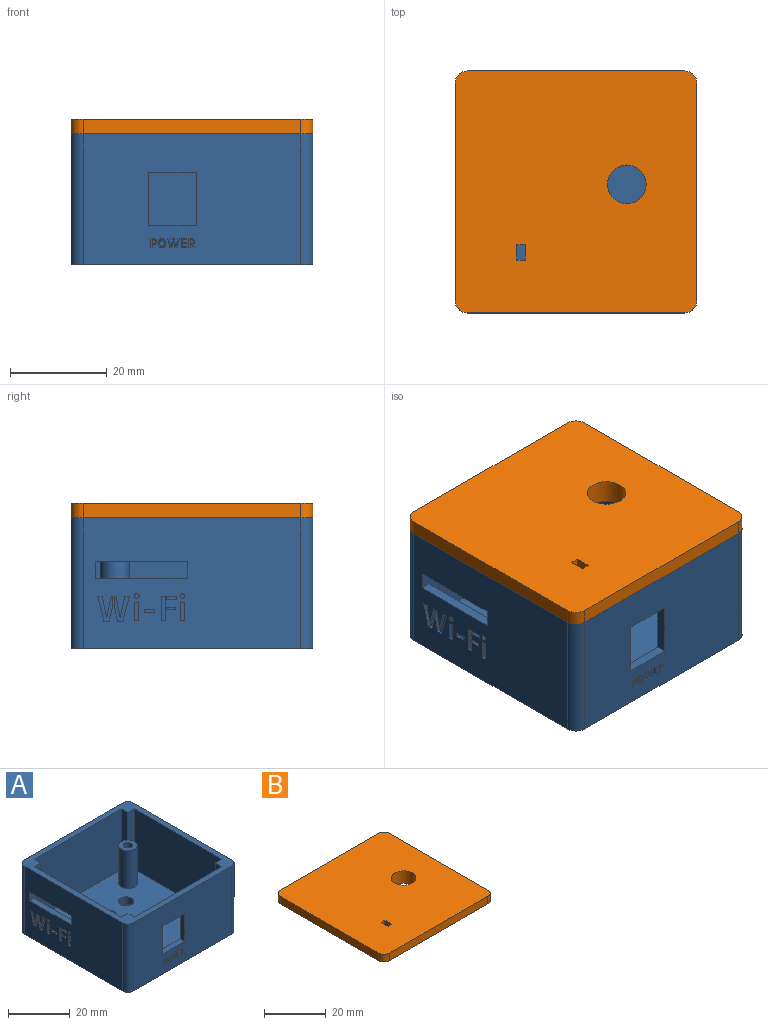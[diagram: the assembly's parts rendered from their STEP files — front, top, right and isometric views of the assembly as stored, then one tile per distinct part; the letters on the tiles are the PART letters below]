
ASSEMBLY  parts=2 mates=1
PART A: 250 faces, bbox 50x50x27 mm
  f0: plane 45x27mm, normal (-1,0,0), area 1117.5mm2, adj f4,f8,f18,f29,f30,f31,f40,f43
  f1: plane 45x27mm, normal (0,-1,0), area 1099.5mm2, adj f4,f8,f25,f26,f27,f28,f40,f41
  f2: plane 40x24mm, normal (1,0,0), area 893.5mm2, adj f4,f11,f17,f18,f29,f30,f31
  f3: plane 24x3mm, normal (1,0,0), area 72mm2, adj f4,f11,f13,f18
  f4: plane 50x50mm, normal (0,0,1), area 414.6mm2, adj f0,f1,f2,f3,f5,f6,f7,f9
  f5: plane 24x3mm, normal (-1,0,0), area 72mm2, adj f4,f11,f13,f16
  f6: plane 45x27mm, normal (1,0,0), area 1215mm2, adj f4,f8,f41,f42
  f7: plane 45x27mm, normal (0,1,0), area 1215mm2, adj f4,f8,f42,f43
  f8: plane 50x50mm, normal (0,0,-1), area 2376.9mm2, adj f0,f1,f6,f7,f32,f33,f34,f35
  f9: plane 24x3mm, normal (1,0,0), area 72mm2, adj f4,f11,f12,f17
  f10: plane 24x3mm, normal (-1,0,0), area 72mm2, adj f4,f11,f12,f14
  f11: plane 46x46mm, normal (0,0,1), area 1962.2mm2, adj f2,f3,f5,f9,f10,f12,f13,f14
  f12: plane 40x24mm, normal (0,1,0), area 851.1mm2, adj f4,f9,f10,f11,f25,f26,f27,f28
  f13: plane 40x24mm, normal (0,-1,0), area 960mm2, adj f3,f4,f5,f11
  f14: plane 24x3mm, normal (0,1,0), area 72mm2, adj f4,f10,f11,f15
  f15: plane 40x24mm, normal (-1,0,0), area 960mm2, adj f4,f11,f14,f16
  f16: plane 24x3mm, normal (0,-1,0), area 72mm2, adj f4,f5,f11,f15
  f17: plane 24x3mm, normal (0,1,0), area 72mm2, adj f2,f4,f9,f11
  f18: plane 24x5mm, normal (0,-1,0), area 79mm2, adj f0,f2,f3,f4,f11,f29,f31
  f19: cylinder r=1.5mm len=16.5mm, axis (0,0,-1), area 155.5mm2, adj f21,f38
  f20: cylinder r=3mm len=15mm, axis (0,0,-1), area 282.7mm2, adj f11,f21
  f21: plane 6x6mm, normal (0,0,1), area 21.2mm2, adj f19,f20
  f22: cylinder r=1.5mm len=16.5mm, axis (0,0,-1), area 155.5mm2, adj f24,f39
  f23: cylinder r=3mm len=15mm, axis (0,0,-1), area 282.7mm2, adj f11,f24
  f24: plane 6x6mm, normal (0,0,1), area 21.2mm2, adj f22,f23
  f25: plane 11x2mm, normal (1,0,0), area 22mm2, adj f1,f12,f26,f28
  f26: plane 9.9x2mm, normal (0,0,1), area 19.8mm2, adj f1,f12,f25,f27
  f27: plane 11x2mm, normal (-1,0,0), area 22mm2, adj f1,f12,f26,f28
  f28: plane 9.9x2mm, normal (0,0,-1), area 19.8mm2, adj f1,f12,f25,f27
  f29: plane 19x2mm, normal (0,0,1), area 38mm2, adj f0,f2,f18,f30
  f30: plane 3.5x2mm, normal (0,1,0), area 7mm2, adj f0,f2,f29,f31
  f31: plane 19x2mm, normal (0,0,-1), area 38mm2, adj f0,f2,f18,f30
  f32: plane 4.4x3mm, normal (1,0,0), area 13.2mm2, adj f8,f11,f33,f35
  f33: plane 3x2.28mm, normal (0,1,0), area 6.8mm2, adj f8,f11,f32,f34
  f34: plane 4.4x3mm, normal (-1,0,0), area 13.2mm2, adj f8,f11,f33,f35
  f35: plane 3x2.28mm, normal (0,-1,0), area 6.8mm2, adj f8,f11,f32,f34
  f36: cylinder r=2.5mm len=5mm, axis (0,0,1), area 47.1mm2, adj f8,f11
  f37: cylinder r=2.5mm len=5mm, axis (0,0,1), area 47.1mm2, adj f8,f11
  f38: cone r=1.5mm half-angle=45deg, axis (0,0,-1), area 30mm2, adj f8,f19
  f39: cone r=1.5mm half-angle=45deg, axis (0,0,-1), area 30mm2, adj f8,f22
  f40: cylinder r=2.5mm len=27mm, axis (0,0,-1), area 106mm2, adj f0,f1,f4,f8
  f41: cylinder r=2.5mm len=27mm, axis (0,0,1), area 106mm2, adj f1,f4,f6,f8
  f42: cylinder r=2.5mm len=27mm, axis (0,0,-1), area 106mm2, adj f4,f6,f7,f8
  f43: cylinder r=2.5mm len=27mm, axis (0,0,1), area 106mm2, adj f0,f4,f7,f8
  f44: plane 3.36x3mm, normal (1,0,0), area 10.1mm2, adj f8,f11,f45,f47
  f45: cylinder r=1.5mm len=3mm, axis (0,0,1), area 23.6mm2, adj f8,f11,f44,f46
  f46: plane 3.36x3mm, normal (-1,0,0), area 10.1mm2, adj f8,f11,f45,f47
  f47: plane 3x1.5mm, normal (0,-1,0), area 4.5mm2, adj f8,f11,f44,f46
  f48: plane 0.5x0.13mm, normal (0,0,-1), area 0.1mm2, adj f1,f49,f69,f70
  f49: plane 0.5x0.23mm, normal (1,0,0), area 0.1mm2, adj f1,f48,f50,f70
  f50: plane 0.5x0.12mm, normal (0,0,1), area 0.1mm2, adj f1,f49,f51,f70
  f51: extruded ~0.5x0.19mm, area 0.1mm2, adj f1,f50,f52,f70
  f52: extruded ~0.5x0.11mm, area 0.1mm2, adj f1,f51,f53,f70
  f53: extruded ~0.5x0.11mm, area 0.1mm2, adj f1,f52,f54,f70
  f54: extruded ~0.5x0.11mm, area 0.1mm2, adj f1,f53,f55,f70
  f55: extruded ~0.5x0.19mm, area 0.1mm2, adj f1,f54,f56,f70
  f56: extruded ~0.5x0.12mm, area 0.1mm2, adj f1,f55,f57,f70
  f57: extruded ~0.5x0.1mm, area 0.1mm2, adj f1,f56,f58,f70
  f58: extruded ~0.5x0.11mm, area 0.1mm2, adj f1,f57,f59,f70
  f59: plane 0.5x0.18mm, normal (0,0,-1), area 0.1mm2, adj f1,f58,f60,f70
  f60: plane 0.5x0.22mm, normal (1,0,0), area 0.1mm2, adj f1,f59,f61,f70
  f61: plane 0.5x0.12mm, normal (0,0,1), area 0.1mm2, adj f1,f60,f62,f70
  f62: extruded ~0.5x0.27mm, area 0.1mm2, adj f1,f61,f63,f70
  f63: extruded ~0.5x0.21mm, area 0.1mm2, adj f1,f62,f64,f70
  f64: extruded ~0.5x0.19mm, area 0.1mm2, adj f1,f63,f65,f70
  f65: extruded ~0.5x0.26mm, area 0.1mm2, adj f1,f64,f66,f70
  f66: extruded ~0.5x0.24mm, area 0.1mm2, adj f1,f65,f67,f70
  f67: extruded ~0.5x0.18mm, area 0.1mm2, adj f1,f66,f68,f70
  f68: extruded ~0.5x0.21mm, area 0.1mm2, adj f1,f67,f69,f70
  f69: extruded ~0.5x0.24mm, area 0.1mm2, adj f1,f48,f68,f70
  f70: plane 1.2x0.78mm, normal (0,-1,0), area 0.5mm2, adj f48,f49,f50,f51,f52,f53,f54,f55
  f71: extruded ~0.5x0.4mm, area 0.2mm2, adj f1,f72,f88,f89
  f72: extruded ~0.5x0.3mm, area 0.2mm2, adj f1,f71,f73,f89
  f73: extruded ~0.5x0.23mm, area 0.1mm2, adj f1,f72,f74,f89
  f74: extruded ~0.5x0.29mm, area 0.2mm2, adj f1,f73,f75,f89
  f75: plane 0.5x0.25mm, normal (-1,0,0), area 0.1mm2, adj f1,f74,f76,f89
  f76: extruded ~0.5x0.16mm, area 0.1mm2, adj f1,f75,f77,f89
  f77: extruded ~0.5x0.13mm, area 0.1mm2, adj f1,f76,f78,f89
  f78: extruded ~0.5x0.21mm, area 0.1mm2, adj f1,f77,f79,f89
  f79: extruded ~0.5x0.31mm, area 0.2mm2, adj f1,f78,f80,f89
  f80: extruded ~0.5x0.31mm, area 0.2mm2, adj f1,f79,f81,f89
  f81: extruded ~0.5x0.21mm, area 0.1mm2, adj f1,f80,f82,f89
  f82: extruded ~0.5x0.13mm, area 0.1mm2, adj f1,f81,f83,f89
  f83: extruded ~0.5x0.16mm, area 0.1mm2, adj f1,f82,f84,f89
  f84: plane 0.5x0.25mm, normal (-1,0,0), area 0.1mm2, adj f1,f83,f85,f89
  f85: extruded ~0.5x0.29mm, area 0.2mm2, adj f1,f84,f86,f89
  f86: extruded ~0.5x0.23mm, area 0.1mm2, adj f1,f85,f87,f89
  f87: extruded ~0.5x0.29mm, area 0.2mm2, adj f1,f86,f88,f89
  f88: extruded ~0.5x0.4mm, area 0.2mm2, adj f1,f71,f87,f89
  f89: plane 1.91x0.73mm, normal (0,-1,0), area 0.6mm2, adj f71,f72,f73,f74,f75,f76,f77,f78
  f90: plane 0.5x0.25mm, normal (1,0,0), area 0.1mm2, adj f1,f91,f107,f108
  f91: extruded ~0.5x0.16mm, area 0.1mm2, adj f1,f90,f92,f108
  f92: extruded ~0.5x0.13mm, area 0.1mm2, adj f1,f91,f93,f108
  f93: extruded ~0.5x0.21mm, area 0.1mm2, adj f1,f92,f94,f108
  f94: extruded ~0.5x0.31mm, area 0.2mm2, adj f1,f93,f95,f108
  f95: extruded ~0.5x0.31mm, area 0.2mm2, adj f1,f94,f96,f108
  f96: extruded ~0.5x0.21mm, area 0.1mm2, adj f1,f95,f97,f108
  f97: extruded ~0.5x0.13mm, area 0.1mm2, adj f1,f96,f98,f108
  f98: extruded ~0.5x0.16mm, area 0.1mm2, adj f1,f97,f99,f108
  f99: plane 0.5x0.25mm, normal (1,0,0), area 0.1mm2, adj f1,f98,f100,f108
  f100: extruded ~0.5x0.29mm, area 0.2mm2, adj f1,f99,f101,f108
  f101: extruded ~0.5x0.23mm, area 0.1mm2, adj f1,f100,f102,f108
  f102: extruded ~0.5x0.3mm, area 0.2mm2, adj f1,f101,f103,f108
  f103: extruded ~0.5x0.4mm, area 0.2mm2, adj f1,f102,f104,f108
  f104: extruded ~0.5x0.4mm, area 0.2mm2, adj f1,f103,f105,f108
  f105: extruded ~0.5x0.29mm, area 0.2mm2, adj f1,f104,f106,f108
  f106: extruded ~0.5x0.23mm, area 0.1mm2, adj f1,f105,f107,f108
  f107: extruded ~0.5x0.29mm, area 0.1mm2, adj f1,f90,f106,f108
  f108: plane 1.91x0.73mm, normal (0,-1,0), area 0.6mm2, adj f90,f91,f92,f93,f94,f95,f96,f97
  f109: plane 1.61x0.5mm, normal (-0.98,0,-0.2), area 0.8mm2, adj f1,f110,f116,f117
  f110: plane 0.5x0.35mm, normal (0,0,-1), area 0.2mm2, adj f1,f109,f111,f117
  f111: plane 1.88x0.5mm, normal (0.97,0,0.24), area 1mm2, adj f1,f110,f112,f117
  f112: plane 0.5x0.4mm, normal (0,0,1), area 0.2mm2, adj f1,f111,f113,f117
  f113: plane 1.2x0.5mm, normal (-0.97,0,0.22), area 0.6mm2, adj f1,f112,f114,f117
  f114: plane 0.68x0.5mm, normal (-1,0,0), area 0.3mm2, adj f1,f113,f115,f117
  f115: plane 0.5x0.12mm, normal (0,0,-1), area 0.1mm2, adj f1,f114,f116,f117
  f116: plane 1.61x0.5mm, normal (0.98,0,-0.21), area 0.8mm2, adj f1,f109,f115,f117
  f117: plane 1.88x1.15mm, normal (0,-1,0), area 1mm2, adj f109,f110,f111,f112,f113,f114,f115,f116
  f118: plane 1.61x0.5mm, normal (0.98,0,-0.22), area 0.8mm2, adj f1,f119,f125,f126
  f119: plane 1.61x0.5mm, normal (-0.98,0,-0.2), area 0.8mm2, adj f1,f118,f120,f126
  f120: plane 0.5x0.12mm, normal (0,0,-1), area 0.1mm2, adj f1,f119,f121,f126
  f121: plane 0.73x0.5mm, normal (1,0,0), area 0.4mm2, adj f1,f120,f122,f126
  f122: plane 1.16x0.5mm, normal (0.98,0,0.21), area 0.6mm2, adj f1,f121,f123,f126
  f123: plane 0.5x0.4mm, normal (0,0,1), area 0.2mm2, adj f1,f122,f124,f126
  f124: plane 1.88x0.51mm, normal (-0.97,0,0.26), area 1mm2, adj f1,f123,f125,f126
  f125: plane 0.5x0.35mm, normal (0,0,-1), area 0.2mm2, adj f1,f118,f124,f126
  f126: plane 1.88x1.16mm, normal (0,-1,0), area 1mm2, adj f118,f119,f120,f121,f122,f123,f124,f125
  f127: plane 1.87x0.5mm, normal (1,0,0), area 0.9mm2, adj f1,f128,f130,f131
  f128: plane 0.5x0.31mm, normal (0,0,1), area 0.2mm2, adj f1,f127,f129,f131
  f129: plane 1.87x0.5mm, normal (-1,0,0), area 0.9mm2, adj f1,f128,f130,f131
  f130: plane 0.5x0.31mm, normal (0,0,-1), area 0.2mm2, adj f1,f127,f129,f131
  f131: plane 1.87x0.31mm, normal (0,-1,0), area 0.6mm2, adj f127,f128,f129,f130
  f132: plane 0.5x0.21mm, normal (-1,0,0), area 0.1mm2, adj f1,f133,f135,f136
  f133: plane 0.68x0.5mm, normal (0,0,-1), area 0.3mm2, adj f1,f132,f134,f136
  f134: plane 0.5x0.21mm, normal (1,0,0), area 0.1mm2, adj f1,f133,f135,f136
  f135: plane 0.68x0.5mm, normal (0,0,1), area 0.3mm2, adj f1,f132,f134,f136
  f136: plane 0.68x0.21mm, normal (0,-1,0), area 0.1mm2, adj f132,f133,f134,f135
  f137: plane 0.5x0.23mm, normal (1,0,0), area 0.1mm2, adj f1,f138,f140,f141
  f138: plane 0.76x0.5mm, normal (0,0,1), area 0.4mm2, adj f1,f137,f139,f141
  f139: plane 0.5x0.23mm, normal (-1,0,0), area 0.1mm2, adj f1,f138,f140,f141
  f140: plane 0.76x0.5mm, normal (0,0,-1), area 0.4mm2, adj f1,f137,f139,f141
  f141: plane 0.76x0.23mm, normal (0,-1,0), area 0.2mm2, adj f137,f138,f139,f140
  f142: plane 0.76x0.5mm, normal (0,0,-1), area 0.4mm2, adj f1,f143,f145,f146
  f143: plane 0.5x0.23mm, normal (1,0,0), area 0.1mm2, adj f1,f142,f144,f146
  f144: plane 0.76x0.5mm, normal (0,0,1), area 0.4mm2, adj f1,f143,f145,f146
  f145: plane 0.5x0.23mm, normal (-1,0,0), area 0.1mm2, adj f1,f142,f144,f146
  f146: plane 0.76x0.23mm, normal (0,-1,0), area 0.2mm2, adj f142,f143,f144,f145
  f147: plane 1.87x0.5mm, normal (1,0,0), area 0.9mm2, adj f1,f148,f150,f151
  f148: plane 0.5x0.3mm, normal (0,0,1), area 0.2mm2, adj f1,f147,f149,f151
  f149: plane 1.87x0.5mm, normal (-1,0,0), area 0.9mm2, adj f1,f148,f150,f151
  f150: plane 0.5x0.3mm, normal (0,0,-1), area 0.2mm2, adj f1,f147,f149,f151
  f151: plane 1.87x0.3mm, normal (0,-1,0), area 0.6mm2, adj f147,f148,f149,f150
  f152: plane 0.74x0.5mm, normal (-0.87,0,-0.5), area 0.4mm2, adj f1,f153,f177,f178
  f153: extruded ~0.5x0.25mm, area 0.2mm2, adj f1,f152,f154,f178
  f154: extruded ~0.5x0.35mm, area 0.2mm2, adj f1,f153,f155,f178
  f155: extruded ~0.5x0.24mm, area 0.1mm2, adj f1,f154,f156,f178
  f156: extruded ~0.5x0.18mm, area 0.1mm2, adj f1,f155,f157,f178
  f157: extruded ~0.5x0.21mm, area 0.1mm2, adj f1,f156,f158,f178
  f158: extruded ~0.5x0.24mm, area 0.1mm2, adj f1,f157,f159,f178
  f159: plane 0.5x0.13mm, normal (0,0,-1), area 0.1mm2, adj f1,f158,f160,f178
  f160: plane 0.5x0.23mm, normal (1,0,0), area 0.1mm2, adj f1,f159,f161,f178
  f161: plane 0.5x0.12mm, normal (0,0,1), area 0.1mm2, adj f1,f160,f162,f178
  f162: extruded ~0.5x0.19mm, area 0.1mm2, adj f1,f161,f163,f178
  f163: extruded ~0.5x0.11mm, area 0.1mm2, adj f1,f162,f164,f178
  f164: extruded ~0.5x0.11mm, area 0.1mm2, adj f1,f163,f165,f178
  f165: extruded ~0.5x0.11mm, area 0.1mm2, adj f1,f164,f166,f178
  f166: extruded ~0.5x0.19mm, area 0.1mm2, adj f1,f165,f167,f178
  f167: extruded ~0.5x0.12mm, area 0.1mm2, adj f1,f166,f168,f178
  f168: extruded ~0.5x0.1mm, area 0.1mm2, adj f1,f167,f169,f178
  f169: extruded ~0.5x0.11mm, area 0.1mm2, adj f1,f168,f170,f178
  f170: plane 0.5x0.17mm, normal (0,0,-1), area 0.1mm2, adj f1,f169,f171,f178
  f171: plane 0.5x0.22mm, normal (1,0,0), area 0.1mm2, adj f1,f170,f172,f178
  f172: plane 0.5x0.09mm, normal (0,0,1), area 0mm2, adj f1,f171,f173,f178
  f173: plane 0.5x0.05mm, normal (0,0,1), area 0mm2, adj f1,f172,f174,f178
  f174: extruded ~0.5x0.03mm, area 0mm2, adj f1,f173,f175,f178
  f175: extruded ~0.5x0.02mm, area 0mm2, adj f1,f174,f176,f178
  f176: plane 0.68x0.5mm, normal (0.89,0,0.46), area 0.4mm2, adj f1,f175,f177,f178
  f177: plane 0.5x0.32mm, normal (0,0,1), area 0.2mm2, adj f1,f152,f176,f178
  f178: plane 1.87x0.86mm, normal (0,-1,0), area 0.7mm2, adj f152,f153,f154,f155,f156,f157,f158,f159
  f179: plane 1.87x0.5mm, normal (1,0,0), area 0.9mm2, adj f1,f180,f182,f183
  f180: plane 0.5x0.3mm, normal (0,0,1), area 0.2mm2, adj f1,f179,f181,f183
  f181: plane 1.87x0.5mm, normal (-1,0,0), area 0.9mm2, adj f1,f180,f182,f183
  f182: plane 0.5x0.3mm, normal (0,0,-1), area 0.2mm2, adj f1,f179,f181,f183
  f183: plane 1.87x0.3mm, normal (0,-1,0), area 0.6mm2, adj f179,f180,f181,f182
  f184: plane 2.2x0.5mm, normal (0,0,-1), area 1.1mm2, adj f0,f185,f187,f188
  f185: plane 0.7x0.5mm, normal (0,-1,0), area 0.3mm2, adj f0,f184,f186,f188
  f186: plane 2.2x0.5mm, normal (0,0,1), area 1.1mm2, adj f0,f185,f187,f188
  f187: plane 0.7x0.5mm, normal (0,1,0), area 0.3mm2, adj f0,f184,f186,f188
  f188: plane 2.2x0.7mm, normal (-1,0,0), area 1.5mm2, adj f184,f185,f186,f187
  f189: extruded ~0.5x0.35mm, area 0.2mm2, adj f0,f190,f196,f197
  f190: extruded ~0.5x0.35mm, area 0.2mm2, adj f0,f189,f191,f197
  f191: extruded ~0.5x0.35mm, area 0.2mm2, adj f0,f190,f192,f197
  f192: extruded ~0.5x0.35mm, area 0.2mm2, adj f0,f191,f193,f197
  f193: extruded ~0.5x0.35mm, area 0.2mm2, adj f0,f192,f194,f197
  f194: extruded ~0.5x0.35mm, area 0.2mm2, adj f0,f193,f195,f197
  f195: extruded ~0.5x0.35mm, area 0.2mm2, adj f0,f194,f196,f197
  f196: extruded ~0.5x0.35mm, area 0.2mm2, adj f0,f189,f195,f197
  f197: plane 0.99x0.99mm, normal (-1,0,0), area 0.8mm2, adj f189,f190,f191,f192,f193,f194,f195,f196
  f198: plane 3.9x0.5mm, normal (0,1,0), area 1.9mm2, adj f0,f199,f201,f202
  f199: plane 0.84x0.5mm, normal (0,0,-1), area 0.4mm2, adj f0,f198,f200,f202
  f200: plane 3.9x0.5mm, normal (0,-1,0), area 1.9mm2, adj f0,f199,f201,f202
  f201: plane 0.84x0.5mm, normal (0,0,1), area 0.4mm2, adj f0,f198,f200,f202
  f202: plane 3.9x0.84mm, normal (-1,0,0), area 3.3mm2, adj f198,f199,f200,f201
  f203: plane 4.39x0.98mm, normal (0,-0.98,-0.22), area 2.3mm2, adj f0,f204,f210,f211
  f204: plane 4.39x0.9mm, normal (0,0.98,-0.2), area 2.2mm2, adj f0,f203,f205,f211
  f205: plane 0.5x0.33mm, normal (0,0,-1), area 0.2mm2, adj f0,f204,f206,f211
  f206: plane 1.98x0.5mm, normal (0,-1,0), area 1mm2, adj f0,f205,f207,f211
  f207: plane 3.14x0.69mm, normal (0,-0.98,0.21), area 1.6mm2, adj f0,f206,f208,f211
  f208: plane 1.08x0.5mm, normal (0,0,1), area 0.5mm2, adj f0,f207,f209,f211
  f209: plane 5.12x1.38mm, normal (0,0.97,0.26), area 2.6mm2, adj f0,f208,f210,f211
  f210: plane 0.94x0.5mm, normal (0,0,-1), area 0.5mm2, adj f0,f203,f209,f211
  f211: plane 5.12x3.14mm, normal (-1,0,0), area 7.4mm2, adj f203,f204,f205,f206,f207,f208,f209,f210
  f212: plane 3.9x0.5mm, normal (0,1,0), area 1.9mm2, adj f0,f213,f215,f216
  f213: plane 0.84x0.5mm, normal (0,0,-1), area 0.4mm2, adj f0,f212,f214,f216
  f214: plane 3.9x0.5mm, normal (0,-1,0), area 1.9mm2, adj f0,f213,f215,f216
  f215: plane 0.84x0.5mm, normal (0,0,1), area 0.4mm2, adj f0,f212,f214,f216
  f216: plane 3.9x0.84mm, normal (-1,0,0), area 3.3mm2, adj f212,f213,f214,f215
  f217: plane 2.06x0.5mm, normal (0,0,-1), area 1mm2, adj f0,f218,f220,f221
  f218: plane 0.63x0.5mm, normal (0,-1,0), area 0.3mm2, adj f0,f217,f219,f221
  f219: plane 2.06x0.5mm, normal (0,0,1), area 1mm2, adj f0,f218,f220,f221
  f220: plane 0.63x0.5mm, normal (0,1,0), area 0.3mm2, adj f0,f217,f219,f221
  f221: plane 2.06x0.63mm, normal (-1,0,0), area 1.3mm2, adj f217,f218,f219,f220
  f222: plane 0.57x0.5mm, normal (0,1,0), area 0.3mm2, adj f0,f223,f225,f226
  f223: plane 1.84x0.5mm, normal (0,0,-1), area 0.9mm2, adj f0,f222,f224,f226
  f224: plane 0.57x0.5mm, normal (0,-1,0), area 0.3mm2, adj f0,f223,f225,f226
  f225: plane 1.84x0.5mm, normal (0,0,1), area 0.9mm2, adj f0,f222,f224,f226
  f226: plane 1.84x0.57mm, normal (-1,0,0), area 1mm2, adj f222,f223,f224,f225
  f227: plane 5.09x0.5mm, normal (0,-1,0), area 2.5mm2, adj f0,f228,f230,f231
  f228: plane 0.84x0.5mm, normal (0,0,1), area 0.4mm2, adj f0,f227,f229,f231
  f229: plane 5.09x0.5mm, normal (0,1,0), area 2.5mm2, adj f0,f228,f230,f231
  f230: plane 0.84x0.5mm, normal (0,0,-1), area 0.4mm2, adj f0,f227,f229,f231
  f231: plane 5.09x0.84mm, normal (-1,0,0), area 4.3mm2, adj f227,f228,f229,f230
  f232: extruded ~0.5x0.35mm, area 0.2mm2, adj f0,f233,f239,f240
  f233: extruded ~0.5x0.35mm, area 0.2mm2, adj f0,f232,f234,f240
  f234: extruded ~0.5x0.35mm, area 0.2mm2, adj f0,f233,f235,f240
  f235: extruded ~0.5x0.35mm, area 0.2mm2, adj f0,f234,f236,f240
  f236: extruded ~0.5x0.35mm, area 0.2mm2, adj f0,f235,f237,f240
  f237: extruded ~0.5x0.35mm, area 0.2mm2, adj f0,f236,f238,f240
  f238: extruded ~0.5x0.35mm, area 0.2mm2, adj f0,f237,f239,f240
  f239: extruded ~0.5x0.35mm, area 0.2mm2, adj f0,f232,f238,f240
  f240: plane 0.99x0.99mm, normal (-1,0,0), area 0.8mm2, adj f232,f233,f234,f235,f236,f237,f238,f239
  f241: plane 4.39x0.9mm, normal (0,0.98,-0.2), area 2.2mm2, adj f0,f242,f248,f249
  f242: plane 0.94x0.5mm, normal (0,0,-1), area 0.5mm2, adj f0,f241,f243,f249
  f243: plane 5.12x1.29mm, normal (0,-0.97,0.24), area 2.6mm2, adj f0,f242,f244,f249
  f244: plane 1.08x0.5mm, normal (0,0,1), area 0.5mm2, adj f0,f243,f245,f249
  f245: plane 3.27x0.75mm, normal (0,0.97,0.22), area 1.7mm2, adj f0,f244,f246,f249
  f246: plane 1.84x0.5mm, normal (0,1,0), area 0.9mm2, adj f0,f245,f247,f249
  f247: plane 0.5x0.33mm, normal (0,0,-1), area 0.2mm2, adj f0,f246,f248,f249
  f248: plane 4.39x0.97mm, normal (0,-0.98,-0.21), area 2.2mm2, adj f0,f241,f247,f249
  f249: plane 5.12x3.13mm, normal (-1,0,0), area 7.4mm2, adj f241,f242,f243,f244,f245,f246,f247,f248
PART B: 28 faces, bbox 50x50x5 mm
  f0: plane 46x46mm, normal (0,0,-1), area 2024.3mm2, adj f1,f3,f9,f10,f11,f12,f13,f14
  f1: plane 3x2mm, normal (1,0,0), area 6mm2, adj f0,f2,f12,f18
  f2: plane 50x50mm, normal (0,0,-1), area 414.6mm2, adj f1,f3,f4,f5,f6,f7,f9,f10
  f3: plane 3x2mm, normal (-1,0,0), area 6mm2, adj f0,f2,f12,f14
  f4: plane 45x3mm, normal (-1,0,0), area 135mm2, adj f2,f8,f24,f27
  f5: plane 45x3mm, normal (0,-1,0), area 135mm2, adj f2,f8,f24,f25
  f6: plane 45x3mm, normal (1,0,0), area 135mm2, adj f2,f8,f25,f26
  f7: plane 45x3mm, normal (0,1,0), area 135mm2, adj f2,f8,f26,f27
  f8: plane 50x50mm, normal (0,0,1), area 2438.9mm2, adj f4,f5,f6,f7,f19,f20,f21,f22
  f9: plane 3x2mm, normal (-1,0,0), area 6mm2, adj f0,f2,f11,f13
  f10: plane 3x2mm, normal (1,0,0), area 6mm2, adj f0,f2,f11,f16
  f11: plane 40x2mm, normal (0,1,0), area 80mm2, adj f0,f2,f9,f10
  f12: plane 40x2mm, normal (0,-1,0), area 80mm2, adj f0,f1,f2,f3
  f13: plane 3x2mm, normal (0,1,0), area 6mm2, adj f0,f2,f9,f15
  f14: plane 3x2mm, normal (0,-1,0), area 6mm2, adj f0,f2,f3,f15
  f15: plane 40x2mm, normal (-1,0,0), area 80mm2, adj f0,f2,f13,f14
  f16: plane 3x2mm, normal (0,1,0), area 6mm2, adj f0,f2,f10,f17
  f17: plane 40x2mm, normal (1,0,0), area 80mm2, adj f0,f2,f16,f18
  f18: plane 3x2mm, normal (0,-1,0), area 6mm2, adj f0,f1,f2,f17
  f19: plane 5x3.2mm, normal (1,0,0), area 16mm2, adj f0,f8,f20,f22
  f20: plane 5x1.7mm, normal (0,1,0), area 8.5mm2, adj f0,f8,f19,f21
  f21: plane 5x3.2mm, normal (-1,0,0), area 16mm2, adj f0,f8,f20,f22
  f22: plane 5x1.7mm, normal (0,-1,0), area 8.5mm2, adj f0,f8,f19,f21
  f23: cylinder r=4mm len=8mm, axis (0,0,1), area 125.7mm2, adj f0,f8
  f24: cylinder r=2.5mm len=3mm, axis (0,0,-1), area 11.8mm2, adj f2,f4,f5,f8
  f25: cylinder r=2.5mm len=3mm, axis (0,0,1), area 11.8mm2, adj f2,f5,f6,f8
  f26: cylinder r=2.5mm len=3mm, axis (0,0,-1), area 11.8mm2, adj f2,f6,f7,f8
  f27: cylinder r=2.5mm len=3mm, axis (0,0,1), area 11.8mm2, adj f2,f4,f7,f8
PLACE A at identity fixed
PLACE B t=(-78.56,-8.24,27)mm
MATE slider B.f24 <-> A.f40  axis (0,0,-1) through (-68.04,8.19,27)mm
